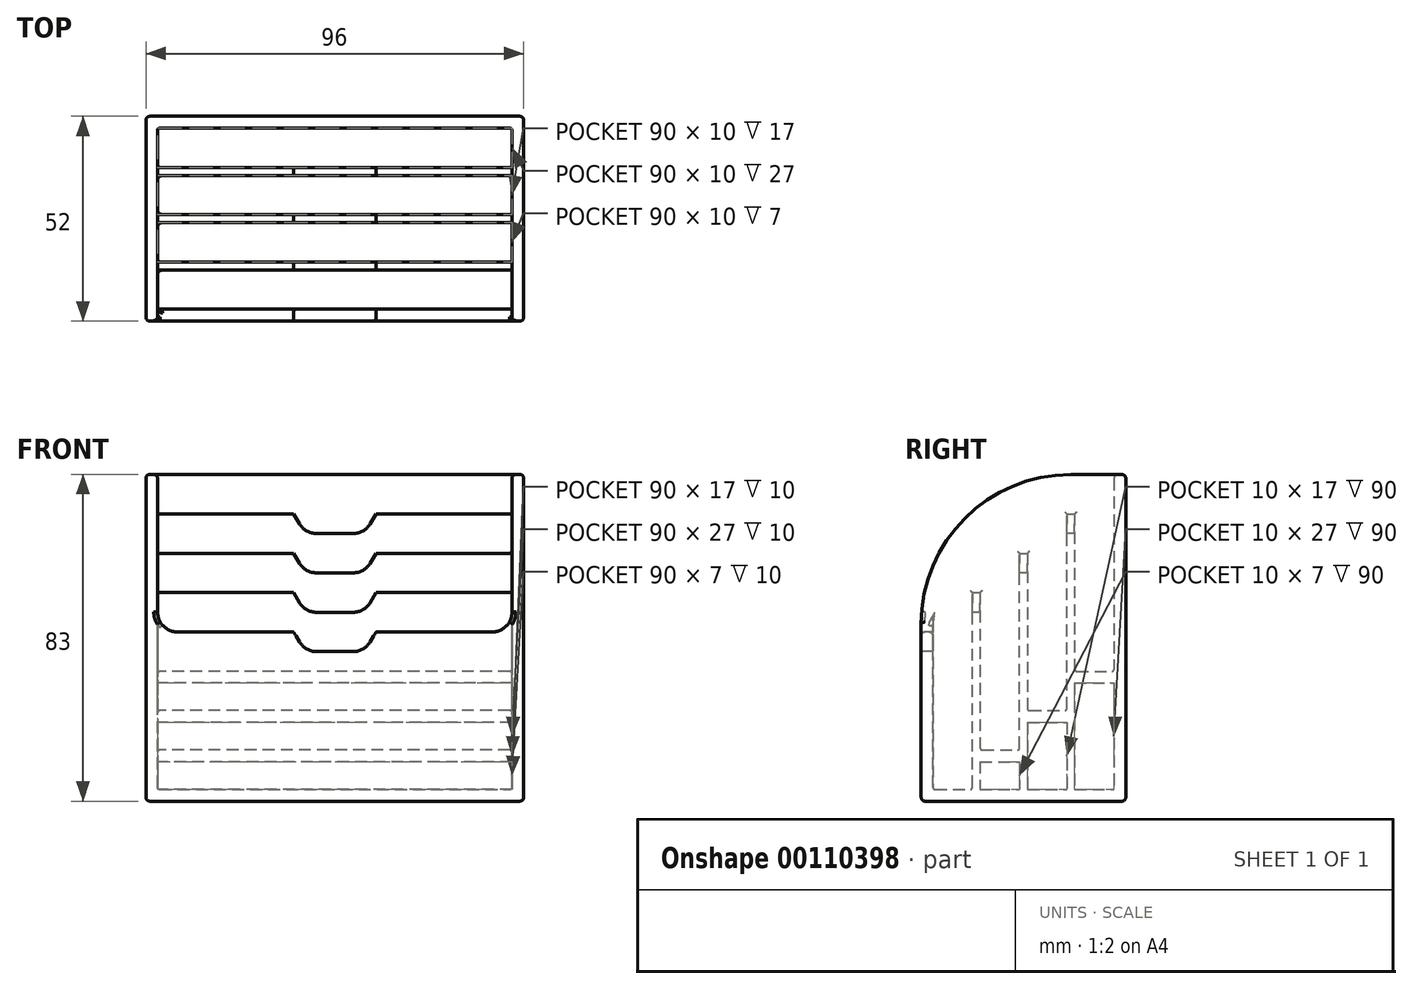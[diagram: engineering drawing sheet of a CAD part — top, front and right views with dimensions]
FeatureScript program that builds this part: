
annotation { "Feature Type Name" : "Feature", "Feature Type Description" : "" }
export const myFeature = defineFeature(function(context is Context, id is Id, definition is map)
    precondition{}
    {
        {
            var Q0;
            Q0=qCreatedBy(makeId("Top.planeOp"),FACE);
            var sketch = newSketch(context, id + "F0", { "sketchPlane" : qUnion([Q0])});
            skLineSegment(sketch, "E0.bottom", {"start": v(0, 0) * mm, "end": v(96, 0) * mm});
            skLineSegment(sketch, "E0.top", {"start": v(0, 52) * mm, "end": v(96, 52) * mm});
            skLineSegment(sketch, "E0.left", {"start": v(0, 0) * mm, "end": v(0, 52) * mm});
            skLineSegment(sketch, "E0.right", {"start": v(96, 0) * mm, "end": v(96, 52) * mm});
            skSolve(sketch);
        }
        {
            var Q0;
            Q0 = qSketchRegion(id + "F0", true);
            extrude(context, id + "F1", {"entities" : qUnion([Q0]), "depth" : 3 * mm});
        }
        {
            var Q0;
            Q0=makeQuery(id+"F1.opExtrude","CAP_FACE",FACE,{"disambiguationData":[OSD([sQuery(id+"F0.wireOp",EDGE,"E0.bottom"),sQuery(id+"F0.wireOp",EDGE,"E0.top"),sQuery(id+"F0.wireOp",EDGE,"E0.left"),sQuery(id+"F0.wireOp",EDGE,"E0.right")])],"isStart":false});
            var sketch = newSketch(context, id + "F2", { "sketchPlane" : qUnion([Q0])});
            skLineSegment(sketch, "E1.bottom", {"start": v(0, 52) * mm, "end": v(96, 52) * mm});
            skLineSegment(sketch, "E1.top", {"start": v(0, 49) * mm, "end": v(96, 49) * mm});
            skLineSegment(sketch, "E1.left", {"start": v(0, 52) * mm, "end": v(0, 49) * mm});
            skLineSegment(sketch, "E1.right", {"start": v(96, 52) * mm, "end": v(96, 49) * mm});
            skSolve(sketch);
        }
        {
            var Q0;
            Q0 = qSketchRegion(id + "F2", true);
            extrude(context, id + "F3", {"entities" : qUnion([Q0]), "operationType" : NewBodyOperationType.ADD, "depth" : 80 * mm});
        }
        {
            var Q0;
            Q0=makeQuery(id+"F1.opExtrude","CAP_FACE",FACE,{"disambiguationData":[OSD([sQuery(id+"F0.wireOp",EDGE,"E0.bottom"),sQuery(id+"F0.wireOp",EDGE,"E0.top"),sQuery(id+"F0.wireOp",EDGE,"E0.left"),sQuery(id+"F0.wireOp",EDGE,"E0.right")])],"isStart":false});
            var sketch = newSketch(context, id + "F4", { "sketchPlane" : qUnion([Q0])});
            skLineSegment(sketch, "E2.bottom", {"start": v(0, 0) * mm, "end": v(96, 0) * mm});
            skLineSegment(sketch, "E2.top", {"start": v(0, 3) * mm, "end": v(96, 3) * mm});
            skLineSegment(sketch, "E2.left", {"start": v(0, 0) * mm, "end": v(0, 3) * mm});
            skLineSegment(sketch, "E2.right", {"start": v(96, 0) * mm, "end": v(96, 3) * mm});
            skSolve(sketch);
        }
        {
            var Q0;
            Q0 = qSketchRegion(id + "F4", true);
            extrude(context, id + "F5", {"entities" : qUnion([Q0]), "operationType" : NewBodyOperationType.ADD, "depth" : 40 * mm});
        }
        {
            var Q0;
            Q0=makeQuery(id+"F5.boolean.opBoolean","MERGE",FACE,{"derivedFrom":[makeQuery(id+"F3.boolean.opBoolean","MERGE",FACE,{"derivedFrom":[makeQuery(id+"F1.opExtrude","SWEPT_FACE",FACE,{"disambiguationData":[OSD([sQuery(id+"F0.wireOp",EDGE,"E0.left")])]}),makeQuery(id+"F3.opExtrude","SWEPT_FACE",FACE,{"disambiguationData":[OSD([sQuery(id+"F2.wireOp",EDGE,"E1.left")])]})]}),makeQuery(id+"F5.opExtrude","SWEPT_FACE",FACE,{"disambiguationData":[OSD([sQuery(id+"F4.wireOp",EDGE,"E2.left")])]})]});
            var sketch = newSketch(context, id + "F6", { "sketchPlane" : qUnion([Q0])});
            skLineSegment(sketch, "E3", {"start": v(-52, 83) * mm, "end": v(-52, 0) * mm});
            skLineSegment(sketch, "E4", {"start": v(-52, 0) * mm, "end": v(0, 0) * mm});
            skLineSegment(sketch, "E5", {"start": v(0, 0) * mm, "end": v(0, 45) * mm});
            skArc(sketch, "E6", {"start": v(0, 45) * mm, "mid": v(-11.13, 71.87) * mm, "end": v(-38, 83) * mm});
            skLineSegment(sketch, "E7", {"start": v(-52, 83) * mm, "end": v(-38, 83) * mm});
            skSolve(sketch);
        }
        {
            var Q0;
            Q0 = qSketchRegion(id + "F6", true);
            extrude(context, id + "F7", {"entities" : qUnion([Q0]), "operationType" : NewBodyOperationType.ADD, "oppositeDirection" : true, "depth" : 3 * mm});
        }
        {
            var Q0;
            Q0=makeQuery(id+"F7.opExtrude","CAP_FACE",FACE,{"disambiguationData":[OSD([sQuery(id+"F6.wireOp",EDGE,"E3"),sQuery(id+"F6.wireOp",EDGE,"E4"),sQuery(id+"F6.wireOp",EDGE,"E5"),sQuery(id+"F6.wireOp",EDGE,"E6"),sQuery(id+"F6.wireOp",EDGE,"E7")])],"isStart":false});
            var sketch = newSketch(context, id + "F8", { "sketchPlane" : qUnion([Q0])});
            skLineSegment(sketch, "E8", {"start": v(13, 3) * mm, "end": v(13, 53) * mm});
            skLineSegment(sketch, "E9", {"start": v(13, 53) * mm, "end": v(15, 53) * mm});
            skLineSegment(sketch, "E10", {"start": v(15, 53) * mm, "end": v(15, 13) * mm});
            skLineSegment(sketch, "E11", {"start": v(15, 13) * mm, "end": v(25, 13) * mm});
            skLineSegment(sketch, "E12", {"start": v(25, 13) * mm, "end": v(25, 63) * mm});
            skLineSegment(sketch, "E13", {"start": v(25, 63) * mm, "end": v(27, 63) * mm});
            skLineSegment(sketch, "E14", {"start": v(27, 63) * mm, "end": v(27, 23) * mm});
            skLineSegment(sketch, "E15", {"start": v(27, 23) * mm, "end": v(37, 23) * mm});
            skLineSegment(sketch, "E16", {"start": v(37, 23) * mm, "end": v(37, 73) * mm});
            skLineSegment(sketch, "E17", {"start": v(37, 73) * mm, "end": v(39, 73) * mm});
            skLineSegment(sketch, "E18", {"start": v(39, 73) * mm, "end": v(39, 33) * mm});
            skLineSegment(sketch, "E19", {"start": v(39, 33) * mm, "end": v(49, 33) * mm});
            skLineSegment(sketch, "E20", {"start": v(49, 33) * mm, "end": v(49, 3) * mm});
            skLineSegment(sketch, "E21", {"start": v(49, 3) * mm, "end": v(13, 3) * mm});
            skLineSegment(sketch, "E22.bottom", {"start": v(15, 10) * mm, "end": v(25, 10) * mm});
            skLineSegment(sketch, "E22.top", {"start": v(15, 3) * mm, "end": v(25, 3) * mm});
            skLineSegment(sketch, "E22.left", {"start": v(15, 10) * mm, "end": v(15, 3) * mm});
            skLineSegment(sketch, "E22.right", {"start": v(25, 10) * mm, "end": v(25, 3) * mm});
            skLineSegment(sketch, "E23.bottom", {"start": v(27, 20) * mm, "end": v(37, 20) * mm});
            skLineSegment(sketch, "E23.top", {"start": v(27, 3) * mm, "end": v(37, 3) * mm});
            skLineSegment(sketch, "E23.left", {"start": v(27, 20) * mm, "end": v(27, 3) * mm});
            skLineSegment(sketch, "E23.right", {"start": v(37, 20) * mm, "end": v(37, 3) * mm});
            skLineSegment(sketch, "E24.bottom", {"start": v(39, 30) * mm, "end": v(49, 30) * mm});
            skLineSegment(sketch, "E24.top", {"start": v(39, 3) * mm, "end": v(49, 3) * mm});
            skLineSegment(sketch, "E24.left", {"start": v(39, 30) * mm, "end": v(39, 3) * mm});
            skLineSegment(sketch, "E24.right", {"start": v(49, 30) * mm, "end": v(49, 3) * mm});
            skSolve(sketch);
        }
        {
            var Q0;
            {var subQ2=sQuery(id+"F8.wireOp",EDGE,"E8");Q0=makeQuery(id+"F8.imprint","IMPRINT",FACE,{"disambiguationData":[TD([[makeQuery(id+"F8.imprint","IMPRINT",EDGE,{"derivedFrom":subQ2}),-1.0]])]});}
            var Q1;
            Q1=makeQuery(id+"F5.boolean.opBoolean","MERGE",FACE,{"derivedFrom":[makeQuery(id+"F3.boolean.opBoolean","MERGE",FACE,{"derivedFrom":[makeQuery(id+"F1.opExtrude","SWEPT_FACE",FACE,{"disambiguationData":[OSD([sQuery(id+"F0.wireOp",EDGE,"E0.right")])]}),makeQuery(id+"F3.opExtrude","SWEPT_FACE",FACE,{"disambiguationData":[OSD([sQuery(id+"F2.wireOp",EDGE,"E1.right")])]})]}),makeQuery(id+"F5.opExtrude","SWEPT_FACE",FACE,{"disambiguationData":[OSD([sQuery(id+"F4.wireOp",EDGE,"E2.right")])]})]});
            extrude(context, id + "F9", {"entities" : qUnion([Q0]), "operationType" : NewBodyOperationType.ADD, "endBound" : BoundingType.UP_TO_SURFACE, "endBoundEntityFace" : qUnion([Q1]), "depth" : 25 * mm});
        }
        {
            var Q0;
            {var subQ0=sQuery(id+"F4.wireOp",EDGE,"E2.right");var subQ1=sQuery(id+"F2.wireOp",EDGE,"E1.right");var subQ2=sQuery(id+"F0.wireOp",EDGE,"E0.right");Q0=makeQuery(id+"F9.boolean.opBoolean","MERGE",FACE,{"derivedFrom":[makeQuery(id+"F5.boolean.opBoolean","MERGE",FACE,{"derivedFrom":[makeQuery(id+"F3.boolean.opBoolean","MERGE",FACE,{"derivedFrom":[makeQuery(id+"F1.opExtrude","SWEPT_FACE",FACE,{"disambiguationData":[OSD([subQ2])]}),makeQuery(id+"F3.opExtrude","SWEPT_FACE",FACE,{"disambiguationData":[OSD([subQ1])]})]}),makeQuery(id+"F5.opExtrude","SWEPT_FACE",FACE,{"disambiguationData":[OSD([subQ0])]})]}),makeQuery(id+"F9.opExtrude","CAP_FACE",FACE,{"disambiguationData":[OSD([subQ2,subQ1,subQ0])],"isStart":false})]});}
            var sketch = newSketch(context, id + "F10", { "sketchPlane" : qUnion([Q0])});
            skLineSegment(sketch, "E25", {"start": v(52, 83) * mm, "end": v(52, 0) * mm});
            skLineSegment(sketch, "E26", {"start": v(52, 0) * mm, "end": v(0, 0) * mm});
            skLineSegment(sketch, "E27", {"start": v(0, 0) * mm, "end": v(0, 43) * mm});
            skLineSegment(sketch, "E28", {"start": v(52, 83) * mm, "end": v(38, 83) * mm});
            skLineSegment(sketch, "E29", {"start": v(0, 43) * mm, "end": v(0, 45) * mm});
            skArc(sketch, "E30", {"start": v(38, 83) * mm, "mid": v(11.13, 71.87) * mm, "end": v(0, 45) * mm});
            skSolve(sketch);
        }
        {
            var Q0;
            Q0 = qSketchRegion(id + "F10", true);
            extrude(context, id + "F11", {"entities" : qUnion([Q0]), "operationType" : NewBodyOperationType.ADD, "oppositeDirection" : true, "depth" : 3 * mm});
        }
        {
            var Q0;
            {var subQ3=sQuery(id+"F2.wireOp",EDGE,"E1.top");var subQ4=sQuery(id+"F6.wireOp",EDGE,"E7");Q0=makeQuery(id+"F11.boolean.opBoolean","INTERSECT",EDGE,{"derivedFrom":[makeQuery(id+"F9.boolean.opBoolean","SPLIT",FACE,{"disambiguationData":[TD([makeQuery(id+"F7.opExtrude","SWEPT_FACE",FACE,{"disambiguationData":[OSD([subQ4])]})])],"derivedFrom":makeQuery(id+"F3.opExtrude","SWEPT_FACE",FACE,{"disambiguationData":[OSD([subQ3])]})}),makeQuery(id+"F11.opExtrude","CAP_FACE",FACE,{"disambiguationData":[OSD([sQuery(id+"F10.wireOp",EDGE,"E25"),sQuery(id+"F10.wireOp",EDGE,"E26"),sQuery(id+"F10.wireOp",EDGE,"E27"),sQuery(id+"F10.wireOp",EDGE,"E28"),sQuery(id+"F10.wireOp",EDGE,"E29"),sQuery(id+"F10.wireOp",EDGE,"E30")])],"isStart":false})]});}
            var Q1;
            Q1=makeQuery(id+"F11.boolean.opBoolean","INTERSECT",EDGE,{"derivedFrom":[makeQuery(id+"F9.opExtrude","SWEPT_FACE",FACE,{"disambiguationData":[OSD([sQuery(id+"F8.wireOp",EDGE,"E18")])]}),makeQuery(id+"F11.opExtrude","CAP_FACE",FACE,{"disambiguationData":[OSD([sQuery(id+"F10.wireOp",EDGE,"E25"),sQuery(id+"F10.wireOp",EDGE,"E26"),sQuery(id+"F10.wireOp",EDGE,"E27"),sQuery(id+"F10.wireOp",EDGE,"E28"),sQuery(id+"F10.wireOp",EDGE,"E29"),sQuery(id+"F10.wireOp",EDGE,"E30")])],"isStart":false})]});
            var Q2;
            Q2=makeQuery(id+"F9.opExtrude","CAP_EDGE",EDGE,{"disambiguationData":[OSD([sQuery(id+"F8.wireOp",EDGE,"E18")])],"isStart":true});
            var Q3;
            {var subQ0=sQuery(id+"F6.wireOp",EDGE,"E7");var subQ1=makeQuery(id+"F7.opExtrude","CAP_FACE",FACE,{"disambiguationData":[OSD([sQuery(id+"F6.wireOp",EDGE,"E3"),sQuery(id+"F6.wireOp",EDGE,"E4"),sQuery(id+"F6.wireOp",EDGE,"E5"),sQuery(id+"F6.wireOp",EDGE,"E6"),subQ0])],"isStart":false});var subQ2=sQuery(id+"F2.wireOp",EDGE,"E1.top");var subQ3=makeQuery(id+"F3.opExtrude","SWEPT_FACE",FACE,{"disambiguationData":[OSD([subQ2])]});Q3=makeQuery(id+"F9.boolean.opBoolean","SPLIT",EDGE,{"disambiguationData":[TD([makeQuery(id+"F7.opExtrude","SWEPT_FACE",FACE,{"disambiguationData":[OSD([subQ0])]})])],"derivedFrom":makeQuery(id+"F7.boolean.opBoolean","INTERSECT",EDGE,{"derivedFrom":[subQ3,subQ1]})});}
            var Q4;
            Q4=makeQuery(id+"F9.opExtrude","CAP_EDGE",EDGE,{"disambiguationData":[OSD([sQuery(id+"F8.wireOp",EDGE,"E16")])],"isStart":true});
            var Q5;
            Q5=makeQuery(id+"F11.boolean.opBoolean","INTERSECT",EDGE,{"derivedFrom":[makeQuery(id+"F9.opExtrude","SWEPT_FACE",FACE,{"disambiguationData":[OSD([sQuery(id+"F8.wireOp",EDGE,"E16")])]}),makeQuery(id+"F11.opExtrude","CAP_FACE",FACE,{"disambiguationData":[OSD([sQuery(id+"F10.wireOp",EDGE,"E25"),sQuery(id+"F10.wireOp",EDGE,"E26"),sQuery(id+"F10.wireOp",EDGE,"E27"),sQuery(id+"F10.wireOp",EDGE,"E28"),sQuery(id+"F10.wireOp",EDGE,"E29"),sQuery(id+"F10.wireOp",EDGE,"E30")])],"isStart":false})]});
            var Q6;
            Q6=makeQuery(id+"F11.boolean.opBoolean","INTERSECT",EDGE,{"derivedFrom":[makeQuery(id+"F9.opExtrude","SWEPT_FACE",FACE,{"disambiguationData":[OSD([sQuery(id+"F8.wireOp",EDGE,"E14")])]}),makeQuery(id+"F11.opExtrude","CAP_FACE",FACE,{"disambiguationData":[OSD([sQuery(id+"F10.wireOp",EDGE,"E25"),sQuery(id+"F10.wireOp",EDGE,"E26"),sQuery(id+"F10.wireOp",EDGE,"E27"),sQuery(id+"F10.wireOp",EDGE,"E28"),sQuery(id+"F10.wireOp",EDGE,"E29"),sQuery(id+"F10.wireOp",EDGE,"E30")])],"isStart":false})]});
            var Q7;
            Q7=makeQuery(id+"F9.opExtrude","CAP_EDGE",EDGE,{"disambiguationData":[OSD([sQuery(id+"F8.wireOp",EDGE,"E14")])],"isStart":true});
            var Q8;
            Q8=makeQuery(id+"F9.opExtrude","CAP_EDGE",EDGE,{"disambiguationData":[OSD([sQuery(id+"F8.wireOp",EDGE,"E10")])],"isStart":true});
            var Q9;
            Q9=makeQuery(id+"F7.boolean.opBoolean","INTERSECT",EDGE,{"derivedFrom":[makeQuery(id+"F5.opExtrude","SWEPT_FACE",FACE,{"disambiguationData":[OSD([sQuery(id+"F4.wireOp",EDGE,"E2.top")])]}),makeQuery(id+"F7.opExtrude","CAP_FACE",FACE,{"disambiguationData":[OSD([sQuery(id+"F6.wireOp",EDGE,"E3"),sQuery(id+"F6.wireOp",EDGE,"E4"),sQuery(id+"F6.wireOp",EDGE,"E5"),sQuery(id+"F6.wireOp",EDGE,"E6"),sQuery(id+"F6.wireOp",EDGE,"E7")])],"isStart":false})]});
            var Q10;
            Q10=makeQuery(id+"F9.opExtrude","CAP_EDGE",EDGE,{"disambiguationData":[OSD([sQuery(id+"F8.wireOp",EDGE,"E12")])],"isStart":true});
            var Q11;
            Q11=makeQuery(id+"F9.opExtrude","CAP_EDGE",EDGE,{"disambiguationData":[OSD([sQuery(id+"F8.wireOp",EDGE,"E8")])],"isStart":true});
            var Q12;
            Q12=makeQuery(id+"F11.boolean.opBoolean","INTERSECT",EDGE,{"derivedFrom":[makeQuery(id+"F9.opExtrude","SWEPT_FACE",FACE,{"disambiguationData":[OSD([sQuery(id+"F8.wireOp",EDGE,"E12")])]}),makeQuery(id+"F11.opExtrude","CAP_FACE",FACE,{"disambiguationData":[OSD([sQuery(id+"F10.wireOp",EDGE,"E25"),sQuery(id+"F10.wireOp",EDGE,"E26"),sQuery(id+"F10.wireOp",EDGE,"E27"),sQuery(id+"F10.wireOp",EDGE,"E28"),sQuery(id+"F10.wireOp",EDGE,"E29"),sQuery(id+"F10.wireOp",EDGE,"E30")])],"isStart":false})]});
            var Q13;
            Q13=makeQuery(id+"F11.boolean.opBoolean","INTERSECT",EDGE,{"derivedFrom":[makeQuery(id+"F9.opExtrude","SWEPT_FACE",FACE,{"disambiguationData":[OSD([sQuery(id+"F8.wireOp",EDGE,"E8")])]}),makeQuery(id+"F11.opExtrude","CAP_FACE",FACE,{"disambiguationData":[OSD([sQuery(id+"F10.wireOp",EDGE,"E25"),sQuery(id+"F10.wireOp",EDGE,"E26"),sQuery(id+"F10.wireOp",EDGE,"E27"),sQuery(id+"F10.wireOp",EDGE,"E28"),sQuery(id+"F10.wireOp",EDGE,"E29"),sQuery(id+"F10.wireOp",EDGE,"E30")])],"isStart":false})]});
            var Q14;
            Q14=makeQuery(id+"F11.boolean.opBoolean","INTERSECT",EDGE,{"derivedFrom":[makeQuery(id+"F5.opExtrude","SWEPT_FACE",FACE,{"disambiguationData":[OSD([sQuery(id+"F4.wireOp",EDGE,"E2.top")])]}),makeQuery(id+"F11.opExtrude","CAP_FACE",FACE,{"disambiguationData":[OSD([sQuery(id+"F10.wireOp",EDGE,"E25"),sQuery(id+"F10.wireOp",EDGE,"E26"),sQuery(id+"F10.wireOp",EDGE,"E27"),sQuery(id+"F10.wireOp",EDGE,"E28"),sQuery(id+"F10.wireOp",EDGE,"E29"),sQuery(id+"F10.wireOp",EDGE,"E30")])],"isStart":false})]});
            var Q15;
            Q15=makeQuery(id+"F11.boolean.opBoolean","INTERSECT",EDGE,{"derivedFrom":[makeQuery(id+"F9.opExtrude","SWEPT_FACE",FACE,{"disambiguationData":[OSD([sQuery(id+"F8.wireOp",EDGE,"E10")])]}),makeQuery(id+"F11.opExtrude","CAP_FACE",FACE,{"disambiguationData":[OSD([sQuery(id+"F10.wireOp",EDGE,"E25"),sQuery(id+"F10.wireOp",EDGE,"E26"),sQuery(id+"F10.wireOp",EDGE,"E27"),sQuery(id+"F10.wireOp",EDGE,"E28"),sQuery(id+"F10.wireOp",EDGE,"E29"),sQuery(id+"F10.wireOp",EDGE,"E30")])],"isStart":false})]});
            var Q16;
            Q16=makeQuery(id+"F9.opExtrude","SWEPT_FACE",FACE,{"disambiguationData":[OSD([sQuery(id+"F8.wireOp",EDGE,"E19")])]});
            var Q17;
            Q17=makeQuery(id+"F9.opExtrude","SWEPT_FACE",FACE,{"disambiguationData":[OSD([sQuery(id+"F8.wireOp",EDGE,"E15")])]});
            var Q18;
            Q18=makeQuery(id+"F9.opExtrude","SWEPT_FACE",FACE,{"disambiguationData":[OSD([sQuery(id+"F8.wireOp",EDGE,"E11")])]});
            var Q19;
            {var subQ2=sQuery(id+"F0.wireOp",EDGE,"E0.right");Q19=makeQuery(id+"F9.boolean.opBoolean","SPLIT",FACE,{"disambiguationData":[TD([makeQuery(id+"F5.opExtrude","SWEPT_FACE",FACE,{"disambiguationData":[OSD([sQuery(id+"F4.wireOp",EDGE,"E2.top")])]})])],"derivedFrom":makeQuery(id+"F1.opExtrude","CAP_FACE",FACE,{"disambiguationData":[OSD([sQuery(id+"F0.wireOp",EDGE,"E0.bottom"),sQuery(id+"F0.wireOp",EDGE,"E0.top"),sQuery(id+"F0.wireOp",EDGE,"E0.left"),subQ2])],"isStart":false})});}
            fillet(context, id + "F12", {"entities" : qUnion([Q0, Q1, Q2, Q3, Q4, Q5, Q6, Q7, Q8, Q9, Q10, Q11, Q12, Q13, Q14, Q15, Q16, Q17, Q18, Q19]), "radius" : 0.5 * mm, "tangentPropagation" : true, "allowEdgeOverflow" : false});
        }
        {
            var Q0;
            Q0=makeQuery(id+"F11.boolean.opBoolean","MERGE",FACE,{"derivedFrom":[makeQuery(id+"F7.boolean.opBoolean","MERGE",FACE,{"derivedFrom":[makeQuery(id+"F5.boolean.opBoolean","MERGE",FACE,{"derivedFrom":[makeQuery(id+"F1.opExtrude","SWEPT_FACE",FACE,{"disambiguationData":[OSD([sQuery(id+"F0.wireOp",EDGE,"E0.bottom")])]}),makeQuery(id+"F5.opExtrude","SWEPT_FACE",FACE,{"disambiguationData":[OSD([sQuery(id+"F4.wireOp",EDGE,"E2.bottom")])]})]}),makeQuery(id+"F7.opExtrude","SWEPT_FACE",FACE,{"disambiguationData":[OSD([sQuery(id+"F6.wireOp",EDGE,"E5")])]})]}),makeQuery(id+"F11.opExtrude","SWEPT_FACE",FACE,{"disambiguationData":[OSD([sQuery(id+"F10.wireOp",EDGE,"E27"),sQuery(id+"F10.wireOp",EDGE,"E29")])]})]});
            var sketch = newSketch(context, id + "F13", { "sketchPlane" : qUnion([Q0])});
            skLineSegment(sketch, "E31", {"start": v(37.5, 43) * mm, "end": v(40.5, 38) * mm});
            skLineSegment(sketch, "E32", {"start": v(40.5, 38) * mm, "end": v(55.5, 38) * mm});
            skLineSegment(sketch, "E33", {"start": v(55.5, 38) * mm, "end": v(58.5, 43) * mm});
            skLineSegment(sketch, "E34", {"start": v(58.5, 43) * mm, "end": v(37.5, 43) * mm});
            skSolve(sketch);
        }
        {
            var Q0;
            Q0 = qSketchRegion(id + "F13", true);
            extrude(context, id + "F14", {"entities" : qUnion([Q0]), "operationType" : NewBodyOperationType.REMOVE, "endBound" : BoundingType.UP_TO_NEXT, "oppositeDirection" : true, "depth" : 25 * mm});
        }
        {
            var Q0;
            Q0=makeQuery(id+"F9.opExtrude","SWEPT_FACE",FACE,{"disambiguationData":[OSD([sQuery(id+"F8.wireOp",EDGE,"E8")])]});
            var sketch = newSketch(context, id + "F15", { "sketchPlane" : qUnion([Q0])});
            skLineSegment(sketch, "E35", {"start": v(37.5, 53) * mm, "end": v(40.5, 48) * mm});
            skLineSegment(sketch, "E36", {"start": v(40.5, 48) * mm, "end": v(55.5, 48) * mm});
            skLineSegment(sketch, "E37", {"start": v(55.5, 48) * mm, "end": v(58.5, 53) * mm});
            skLineSegment(sketch, "E38", {"start": v(58.5, 53) * mm, "end": v(37.5, 53) * mm});
            skSolve(sketch);
        }
        {
            var Q0;
            Q0 = qSketchRegion(id + "F15", true);
            extrude(context, id + "F16", {"entities" : qUnion([Q0]), "operationType" : NewBodyOperationType.REMOVE, "endBound" : BoundingType.UP_TO_NEXT, "oppositeDirection" : true, "depth" : 25 * mm});
        }
        {
            var Q0;
            Q0=makeQuery(id+"F9.opExtrude","SWEPT_FACE",FACE,{"disambiguationData":[OSD([sQuery(id+"F8.wireOp",EDGE,"E12")])]});
            var sketch = newSketch(context, id + "F17", { "sketchPlane" : qUnion([Q0])});
            skLineSegment(sketch, "E39", {"start": v(37.5, 63) * mm, "end": v(40.5, 58) * mm});
            skLineSegment(sketch, "E40", {"start": v(40.5, 58) * mm, "end": v(55.5, 58) * mm});
            skLineSegment(sketch, "E41", {"start": v(55.5, 58) * mm, "end": v(58.5, 63) * mm});
            skLineSegment(sketch, "E42", {"start": v(58.5, 63) * mm, "end": v(37.5, 63) * mm});
            skSolve(sketch);
        }
        {
            var Q0;
            Q0 = qSketchRegion(id + "F17", true);
            extrude(context, id + "F18", {"entities" : qUnion([Q0]), "operationType" : NewBodyOperationType.REMOVE, "endBound" : BoundingType.UP_TO_NEXT, "oppositeDirection" : true, "depth" : 25 * mm});
        }
        {
            var Q0;
            Q0=makeQuery(id+"F9.opExtrude","SWEPT_FACE",FACE,{"disambiguationData":[OSD([sQuery(id+"F8.wireOp",EDGE,"E16")])]});
            var sketch = newSketch(context, id + "F19", { "sketchPlane" : qUnion([Q0])});
            skLineSegment(sketch, "E43", {"start": v(37.5, 73) * mm, "end": v(40.5, 68) * mm});
            skLineSegment(sketch, "E44", {"start": v(40.5, 68) * mm, "end": v(55.5, 68) * mm});
            skLineSegment(sketch, "E45", {"start": v(55.5, 68) * mm, "end": v(58.5, 73) * mm});
            skLineSegment(sketch, "E46", {"start": v(58.5, 73) * mm, "end": v(37.5, 73) * mm});
            skSolve(sketch);
        }
        {
            var Q0;
            Q0 = qSketchRegion(id + "F19", true);
            extrude(context, id + "F20", {"entities" : qUnion([Q0]), "operationType" : NewBodyOperationType.REMOVE, "endBound" : BoundingType.UP_TO_NEXT, "oppositeDirection" : true, "depth" : 25 * mm});
        }
        {
            var Q0;
            Q0=makeQuery(id+"F7.boolean.opBoolean","INTERSECT",EDGE,{"derivedFrom":[makeQuery(id+"F5.opExtrude","CAP_FACE",FACE,{"disambiguationData":[OSD([sQuery(id+"F4.wireOp",EDGE,"E2.bottom"),sQuery(id+"F4.wireOp",EDGE,"E2.top"),sQuery(id+"F4.wireOp",EDGE,"E2.left"),sQuery(id+"F4.wireOp",EDGE,"E2.right")])],"isStart":false}),makeQuery(id+"F7.opExtrude","CAP_FACE",FACE,{"disambiguationData":[OSD([sQuery(id+"F6.wireOp",EDGE,"E3"),sQuery(id+"F6.wireOp",EDGE,"E4"),sQuery(id+"F6.wireOp",EDGE,"E5"),sQuery(id+"F6.wireOp",EDGE,"E6"),sQuery(id+"F6.wireOp",EDGE,"E7")])],"isStart":false})]});
            var Q1;
            Q1=makeQuery(id+"F11.boolean.opBoolean","INTERSECT",EDGE,{"derivedFrom":[makeQuery(id+"F5.opExtrude","CAP_FACE",FACE,{"disambiguationData":[OSD([sQuery(id+"F4.wireOp",EDGE,"E2.bottom"),sQuery(id+"F4.wireOp",EDGE,"E2.top"),sQuery(id+"F4.wireOp",EDGE,"E2.left"),sQuery(id+"F4.wireOp",EDGE,"E2.right")])],"isStart":false}),makeQuery(id+"F11.opExtrude","CAP_FACE",FACE,{"disambiguationData":[OSD([sQuery(id+"F10.wireOp",EDGE,"E25"),sQuery(id+"F10.wireOp",EDGE,"E26"),sQuery(id+"F10.wireOp",EDGE,"E27"),sQuery(id+"F10.wireOp",EDGE,"E28"),sQuery(id+"F10.wireOp",EDGE,"E29"),sQuery(id+"F10.wireOp",EDGE,"E30")])],"isStart":false})]});
            fillet(context, id + "F21", {"entities" : qUnion([Q0, Q1]), "radius" : 5 * mm, "tangentPropagation" : true, "allowEdgeOverflow" : false});
        }
        {
            var Q0;
            Q0=makeQuery(id+"F14.boolean.opBoolean","COPY",EDGE,{"derivedFrom":makeQuery(id+"F14.opExtrude","SWEPT_EDGE",EDGE,{"disambiguationData":[OSD([sQuery(id+"F4.wireOp",EDGE,"E2.bottom"),sQuery(id+"F13.wireOp",EDGE,"E31"),sQuery(id+"F13.wireOp",EDGE,"E34")])]})});
            var Q1;
            Q1=makeQuery(id+"F14.boolean.opBoolean","COPY",EDGE,{"derivedFrom":makeQuery(id+"F14.opExtrude","SWEPT_EDGE",EDGE,{"disambiguationData":[OSD([sQuery(id+"F13.wireOp",EDGE,"E31"),sQuery(id+"F13.wireOp",EDGE,"E32")])]})});
            var Q2;
            Q2=makeQuery(id+"F14.boolean.opBoolean","COPY",EDGE,{"derivedFrom":makeQuery(id+"F14.opExtrude","SWEPT_EDGE",EDGE,{"disambiguationData":[OSD([sQuery(id+"F13.wireOp",EDGE,"E32"),sQuery(id+"F13.wireOp",EDGE,"E33")])]})});
            var Q3;
            Q3=makeQuery(id+"F14.boolean.opBoolean","COPY",EDGE,{"derivedFrom":makeQuery(id+"F14.opExtrude","SWEPT_EDGE",EDGE,{"disambiguationData":[OSD([sQuery(id+"F4.wireOp",EDGE,"E2.bottom"),sQuery(id+"F13.wireOp",EDGE,"E33"),sQuery(id+"F13.wireOp",EDGE,"E34")])]})});
            fillet(context, id + "F22", {"entities" : qUnion([Q0, Q1, Q2, Q3]), "radius" : 5 * mm, "tangentPropagation" : true, "allowEdgeOverflow" : false});
        }
        {
            var Q0;
            Q0=makeQuery(id+"F16.boolean.opBoolean","COPY",EDGE,{"derivedFrom":makeQuery(id+"F16.opExtrude","SWEPT_EDGE",EDGE,{"disambiguationData":[OSD([sQuery(id+"F8.wireOp",EDGE,"E8"),sQuery(id+"F8.wireOp",EDGE,"E9"),sQuery(id+"F15.wireOp",EDGE,"E35"),sQuery(id+"F15.wireOp",EDGE,"E38")])]})});
            var Q1;
            Q1=makeQuery(id+"F16.boolean.opBoolean","COPY",EDGE,{"derivedFrom":makeQuery(id+"F16.opExtrude","SWEPT_EDGE",EDGE,{"disambiguationData":[OSD([sQuery(id+"F15.wireOp",EDGE,"E35"),sQuery(id+"F15.wireOp",EDGE,"E36")])]})});
            var Q2;
            Q2=makeQuery(id+"F18.boolean.opBoolean","COPY",EDGE,{"derivedFrom":makeQuery(id+"F18.opExtrude","SWEPT_EDGE",EDGE,{"disambiguationData":[OSD([sQuery(id+"F8.wireOp",EDGE,"E12"),sQuery(id+"F8.wireOp",EDGE,"E13"),sQuery(id+"F17.wireOp",EDGE,"E39"),sQuery(id+"F17.wireOp",EDGE,"E42")])]})});
            var Q3;
            Q3=makeQuery(id+"F18.boolean.opBoolean","COPY",EDGE,{"derivedFrom":makeQuery(id+"F18.opExtrude","SWEPT_EDGE",EDGE,{"disambiguationData":[OSD([sQuery(id+"F17.wireOp",EDGE,"E39"),sQuery(id+"F17.wireOp",EDGE,"E40")])]})});
            var Q4;
            Q4=makeQuery(id+"F20.boolean.opBoolean","COPY",EDGE,{"derivedFrom":makeQuery(id+"F20.opExtrude","SWEPT_EDGE",EDGE,{"disambiguationData":[OSD([sQuery(id+"F19.wireOp",EDGE,"E43"),sQuery(id+"F19.wireOp",EDGE,"E44")])]})});
            var Q5;
            Q5=makeQuery(id+"F20.boolean.opBoolean","COPY",EDGE,{"derivedFrom":makeQuery(id+"F20.opExtrude","SWEPT_EDGE",EDGE,{"disambiguationData":[OSD([sQuery(id+"F8.wireOp",EDGE,"E16"),sQuery(id+"F8.wireOp",EDGE,"E17"),sQuery(id+"F19.wireOp",EDGE,"E43"),sQuery(id+"F19.wireOp",EDGE,"E46")])]})});
            var Q6;
            Q6=makeQuery(id+"F20.boolean.opBoolean","COPY",EDGE,{"derivedFrom":makeQuery(id+"F20.opExtrude","SWEPT_EDGE",EDGE,{"disambiguationData":[OSD([sQuery(id+"F8.wireOp",EDGE,"E16"),sQuery(id+"F8.wireOp",EDGE,"E17"),sQuery(id+"F19.wireOp",EDGE,"E45"),sQuery(id+"F19.wireOp",EDGE,"E46")])]})});
            var Q7;
            Q7=makeQuery(id+"F20.boolean.opBoolean","COPY",EDGE,{"derivedFrom":makeQuery(id+"F20.opExtrude","SWEPT_EDGE",EDGE,{"disambiguationData":[OSD([sQuery(id+"F19.wireOp",EDGE,"E44"),sQuery(id+"F19.wireOp",EDGE,"E45")])]})});
            var Q8;
            Q8=makeQuery(id+"F18.boolean.opBoolean","COPY",EDGE,{"derivedFrom":makeQuery(id+"F18.opExtrude","SWEPT_EDGE",EDGE,{"disambiguationData":[OSD([sQuery(id+"F17.wireOp",EDGE,"E40"),sQuery(id+"F17.wireOp",EDGE,"E41")])]})});
            var Q9;
            Q9=makeQuery(id+"F18.boolean.opBoolean","COPY",EDGE,{"derivedFrom":makeQuery(id+"F18.opExtrude","SWEPT_EDGE",EDGE,{"disambiguationData":[OSD([sQuery(id+"F8.wireOp",EDGE,"E12"),sQuery(id+"F8.wireOp",EDGE,"E13"),sQuery(id+"F17.wireOp",EDGE,"E41"),sQuery(id+"F17.wireOp",EDGE,"E42")])]})});
            var Q10;
            Q10=makeQuery(id+"F16.boolean.opBoolean","COPY",EDGE,{"derivedFrom":makeQuery(id+"F16.opExtrude","SWEPT_EDGE",EDGE,{"disambiguationData":[OSD([sQuery(id+"F8.wireOp",EDGE,"E8"),sQuery(id+"F8.wireOp",EDGE,"E9"),sQuery(id+"F15.wireOp",EDGE,"E37"),sQuery(id+"F15.wireOp",EDGE,"E38")])]})});
            var Q11;
            Q11=makeQuery(id+"F16.boolean.opBoolean","COPY",EDGE,{"derivedFrom":makeQuery(id+"F16.opExtrude","SWEPT_EDGE",EDGE,{"disambiguationData":[OSD([sQuery(id+"F15.wireOp",EDGE,"E36"),sQuery(id+"F15.wireOp",EDGE,"E37")])]})});
            fillet(context, id + "F23", {"entities" : qUnion([Q0, Q1, Q2, Q3, Q4, Q5, Q6, Q7, Q8, Q9, Q10, Q11]), "radius" : 5 * mm, "tangentPropagation" : true, "allowEdgeOverflow" : false});
        }
        {
            var Q0;
            Q0=makeQuery(id+"F7.opExtrude","CAP_EDGE",EDGE,{"disambiguationData":[OSD([sQuery(id+"F6.wireOp",EDGE,"E6")])],"isStart":false});
            var Q1;
            {var subQ1=sQuery(id+"F4.wireOp",EDGE,"E2.bottom");Q1=makeQuery(id+"F14.boolean.opBoolean","SPLIT",EDGE,{"disambiguationData":[TD([makeQuery(id+"F14.opExtrude","SWEPT_FACE",FACE,{"disambiguationData":[OSD([sQuery(id+"F13.wireOp",EDGE,"E31")])]})])],"derivedFrom":makeQuery(id+"F5.opExtrude","CAP_EDGE",EDGE,{"disambiguationData":[OSD([subQ1])],"isStart":false})});}
            var Q2;
            {var subQ0=sQuery(id+"F4.wireOp",EDGE,"E2.top");Q2=makeQuery(id+"F14.boolean.opBoolean","SPLIT",EDGE,{"disambiguationData":[TD([makeQuery(id+"F14.opExtrude","SWEPT_FACE",FACE,{"disambiguationData":[OSD([sQuery(id+"F13.wireOp",EDGE,"E31")])]})])],"derivedFrom":makeQuery(id+"F5.opExtrude","CAP_EDGE",EDGE,{"disambiguationData":[OSD([subQ0])],"isStart":false})});}
            var Q3;
            Q3=makeQuery(id+"F7.boolean.opBoolean","MERGE",EDGE,{"derivedFrom":[makeQuery(id+"F5.boolean.opBoolean","MERGE",EDGE,{"derivedFrom":[makeQuery(id+"F1.opExtrude","SWEPT_EDGE",EDGE,{"disambiguationData":[OSD([sQuery(id+"F0.wireOp",EDGE,"E0.bottom"),sQuery(id+"F0.wireOp",EDGE,"E0.left")])]}),makeQuery(id+"F5.opExtrude","SWEPT_EDGE",EDGE,{"disambiguationData":[OSD([sQuery(id+"F4.wireOp",EDGE,"E2.bottom"),sQuery(id+"F4.wireOp",EDGE,"E2.left")])]})]}),makeQuery(id+"F7.opExtrude","CAP_EDGE",EDGE,{"disambiguationData":[OSD([sQuery(id+"F6.wireOp",EDGE,"E5")])],"isStart":true})]});
            var Q4;
            Q4=makeQuery(id+"F11.boolean.opBoolean","MERGE",EDGE,{"derivedFrom":[makeQuery(id+"F5.boolean.opBoolean","MERGE",EDGE,{"derivedFrom":[makeQuery(id+"F1.opExtrude","SWEPT_EDGE",EDGE,{"disambiguationData":[OSD([sQuery(id+"F0.wireOp",EDGE,"E0.bottom"),sQuery(id+"F0.wireOp",EDGE,"E0.right")])]}),makeQuery(id+"F5.opExtrude","SWEPT_EDGE",EDGE,{"disambiguationData":[OSD([sQuery(id+"F4.wireOp",EDGE,"E2.bottom"),sQuery(id+"F4.wireOp",EDGE,"E2.right")])]})]}),makeQuery(id+"F11.opExtrude","CAP_EDGE",EDGE,{"disambiguationData":[OSD([sQuery(id+"F10.wireOp",EDGE,"E27"),sQuery(id+"F10.wireOp",EDGE,"E29")])],"isStart":true})]});
            var Q5;
            Q5=makeQuery(id+"F3.opExtrude","CAP_EDGE",EDGE,{"disambiguationData":[OSD([sQuery(id+"F2.wireOp",EDGE,"E1.bottom")])],"isStart":false});
            var Q6;
            Q6=makeQuery(id+"F3.boolean.opBoolean","MERGE",EDGE,{"derivedFrom":[makeQuery(id+"F1.opExtrude","SWEPT_EDGE",EDGE,{"disambiguationData":[OSD([sQuery(id+"F0.wireOp",EDGE,"E0.top"),sQuery(id+"F0.wireOp",EDGE,"E0.right")])]}),makeQuery(id+"F3.opExtrude","SWEPT_EDGE",EDGE,{"disambiguationData":[OSD([sQuery(id+"F2.wireOp",EDGE,"E1.bottom"),sQuery(id+"F2.wireOp",EDGE,"E1.right")])]})]});
            var Q7;
            Q7=makeQuery(id+"F3.boolean.opBoolean","MERGE",EDGE,{"derivedFrom":[makeQuery(id+"F1.opExtrude","SWEPT_EDGE",EDGE,{"disambiguationData":[OSD([sQuery(id+"F0.wireOp",EDGE,"E0.top"),sQuery(id+"F0.wireOp",EDGE,"E0.left")])]}),makeQuery(id+"F3.opExtrude","SWEPT_EDGE",EDGE,{"disambiguationData":[OSD([sQuery(id+"F2.wireOp",EDGE,"E1.bottom"),sQuery(id+"F2.wireOp",EDGE,"E1.left")])]})]});
            var Q8;
            Q8=makeQuery(id+"F1.opExtrude","CAP_FACE",FACE,{"disambiguationData":[OSD([sQuery(id+"F0.wireOp",EDGE,"E0.bottom"),sQuery(id+"F0.wireOp",EDGE,"E0.top"),sQuery(id+"F0.wireOp",EDGE,"E0.left"),sQuery(id+"F0.wireOp",EDGE,"E0.right")])],"isStart":true});
            fillet(context, id + "F24", {"entities" : qUnion([Q0, Q1, Q2, Q3, Q4, Q5, Q6, Q7, Q8]), "radius" : 1 * mm, "tangentPropagation" : true, "allowEdgeOverflow" : false});
        }
        {
            var Q0;
            {var subQ0=sQuery(id+"F8.wireOp",EDGE,"E8");var subQ1=sQuery(id+"F8.wireOp",EDGE,"E9");Q0=makeQuery(id+"F16.boolean.opBoolean","SPLIT",EDGE,{"disambiguationData":[TD([makeQuery(id+"F12.opFillet","BLEND_FACE",FACE,{"disambiguationData":[OSD([subQ0])]})])],"derivedFrom":makeQuery(id+"F9.opExtrude","SWEPT_EDGE",EDGE,{"disambiguationData":[OSD([subQ0,subQ1])]})});}
            var Q1;
            {var subQ0=sQuery(id+"F8.wireOp",EDGE,"E9");var subQ1=sQuery(id+"F8.wireOp",EDGE,"E10");Q1=makeQuery(id+"F16.boolean.opBoolean","SPLIT",EDGE,{"disambiguationData":[TD([makeQuery(id+"F12.opFillet","BLEND_FACE",FACE,{"disambiguationData":[OSD([subQ1])]})])],"derivedFrom":makeQuery(id+"F9.opExtrude","SWEPT_EDGE",EDGE,{"disambiguationData":[OSD([subQ0,subQ1])]})});}
            var Q2;
            {var subQ0=sQuery(id+"F8.wireOp",EDGE,"E12");var subQ1=sQuery(id+"F8.wireOp",EDGE,"E13");Q2=makeQuery(id+"F18.boolean.opBoolean","SPLIT",EDGE,{"disambiguationData":[TD([makeQuery(id+"F12.opFillet","BLEND_FACE",FACE,{"disambiguationData":[OSD([subQ0])]})])],"derivedFrom":makeQuery(id+"F9.opExtrude","SWEPT_EDGE",EDGE,{"disambiguationData":[OSD([subQ0,subQ1])]})});}
            var Q3;
            {var subQ0=sQuery(id+"F8.wireOp",EDGE,"E13");var subQ1=sQuery(id+"F8.wireOp",EDGE,"E14");Q3=makeQuery(id+"F18.boolean.opBoolean","SPLIT",EDGE,{"disambiguationData":[TD([makeQuery(id+"F12.opFillet","BLEND_FACE",FACE,{"disambiguationData":[OSD([subQ1])]})])],"derivedFrom":makeQuery(id+"F9.opExtrude","SWEPT_EDGE",EDGE,{"disambiguationData":[OSD([subQ0,subQ1])]})});}
            var Q4;
            {var subQ0=sQuery(id+"F8.wireOp",EDGE,"E16");var subQ1=sQuery(id+"F8.wireOp",EDGE,"E17");Q4=makeQuery(id+"F20.boolean.opBoolean","SPLIT",EDGE,{"disambiguationData":[TD([makeQuery(id+"F12.opFillet","BLEND_FACE",FACE,{"disambiguationData":[OSD([subQ0])]})])],"derivedFrom":makeQuery(id+"F9.opExtrude","SWEPT_EDGE",EDGE,{"disambiguationData":[OSD([subQ0,subQ1])]})});}
            var Q5;
            {var subQ0=sQuery(id+"F8.wireOp",EDGE,"E17");var subQ1=sQuery(id+"F8.wireOp",EDGE,"E18");Q5=makeQuery(id+"F20.boolean.opBoolean","SPLIT",EDGE,{"disambiguationData":[TD([makeQuery(id+"F12.opFillet","BLEND_FACE",FACE,{"disambiguationData":[OSD([subQ1])]})])],"derivedFrom":makeQuery(id+"F9.opExtrude","SWEPT_EDGE",EDGE,{"disambiguationData":[OSD([subQ0,subQ1])]})});}
            var Q6;
            Q6=makeQuery(id+"F9.opExtrude","CAP_EDGE",EDGE,{"disambiguationData":[OSD([sQuery(id+"F8.wireOp",EDGE,"E9")])],"isStart":true});
            var Q7;
            Q7=makeQuery(id+"F9.opExtrude","CAP_EDGE",EDGE,{"disambiguationData":[OSD([sQuery(id+"F8.wireOp",EDGE,"E13")])],"isStart":true});
            var Q8;
            Q8=makeQuery(id+"F9.opExtrude","CAP_EDGE",EDGE,{"disambiguationData":[OSD([sQuery(id+"F8.wireOp",EDGE,"E17")])],"isStart":true});
            var Q9;
            Q9=makeQuery(id+"F11.boolean.opBoolean","INTERSECT",EDGE,{"derivedFrom":[makeQuery(id+"F9.opExtrude","SWEPT_FACE",FACE,{"disambiguationData":[OSD([sQuery(id+"F8.wireOp",EDGE,"E17")])]}),makeQuery(id+"F11.opExtrude","CAP_FACE",FACE,{"disambiguationData":[OSD([sQuery(id+"F10.wireOp",EDGE,"E25"),sQuery(id+"F10.wireOp",EDGE,"E26"),sQuery(id+"F10.wireOp",EDGE,"E27"),sQuery(id+"F10.wireOp",EDGE,"E28"),sQuery(id+"F10.wireOp",EDGE,"E29"),sQuery(id+"F10.wireOp",EDGE,"E30")])],"isStart":false})]});
            var Q10;
            Q10=makeQuery(id+"F11.boolean.opBoolean","INTERSECT",EDGE,{"derivedFrom":[makeQuery(id+"F9.opExtrude","SWEPT_FACE",FACE,{"disambiguationData":[OSD([sQuery(id+"F8.wireOp",EDGE,"E13")])]}),makeQuery(id+"F11.opExtrude","CAP_FACE",FACE,{"disambiguationData":[OSD([sQuery(id+"F10.wireOp",EDGE,"E25"),sQuery(id+"F10.wireOp",EDGE,"E26"),sQuery(id+"F10.wireOp",EDGE,"E27"),sQuery(id+"F10.wireOp",EDGE,"E28"),sQuery(id+"F10.wireOp",EDGE,"E29"),sQuery(id+"F10.wireOp",EDGE,"E30")])],"isStart":false})]});
            var Q11;
            Q11=makeQuery(id+"F11.boolean.opBoolean","INTERSECT",EDGE,{"derivedFrom":[makeQuery(id+"F9.opExtrude","SWEPT_FACE",FACE,{"disambiguationData":[OSD([sQuery(id+"F8.wireOp",EDGE,"E9")])]}),makeQuery(id+"F11.opExtrude","CAP_FACE",FACE,{"disambiguationData":[OSD([sQuery(id+"F10.wireOp",EDGE,"E25"),sQuery(id+"F10.wireOp",EDGE,"E26"),sQuery(id+"F10.wireOp",EDGE,"E27"),sQuery(id+"F10.wireOp",EDGE,"E28"),sQuery(id+"F10.wireOp",EDGE,"E29"),sQuery(id+"F10.wireOp",EDGE,"E30")])],"isStart":false})]});
            fillet(context, id + "F25", {"entities" : qUnion([Q0, Q1, Q2, Q3, Q4, Q5, Q6, Q7, Q8, Q9, Q10, Q11]), "radius" : 0.5 * mm, "tangentPropagation" : true, "allowEdgeOverflow" : false});
        }
    });
